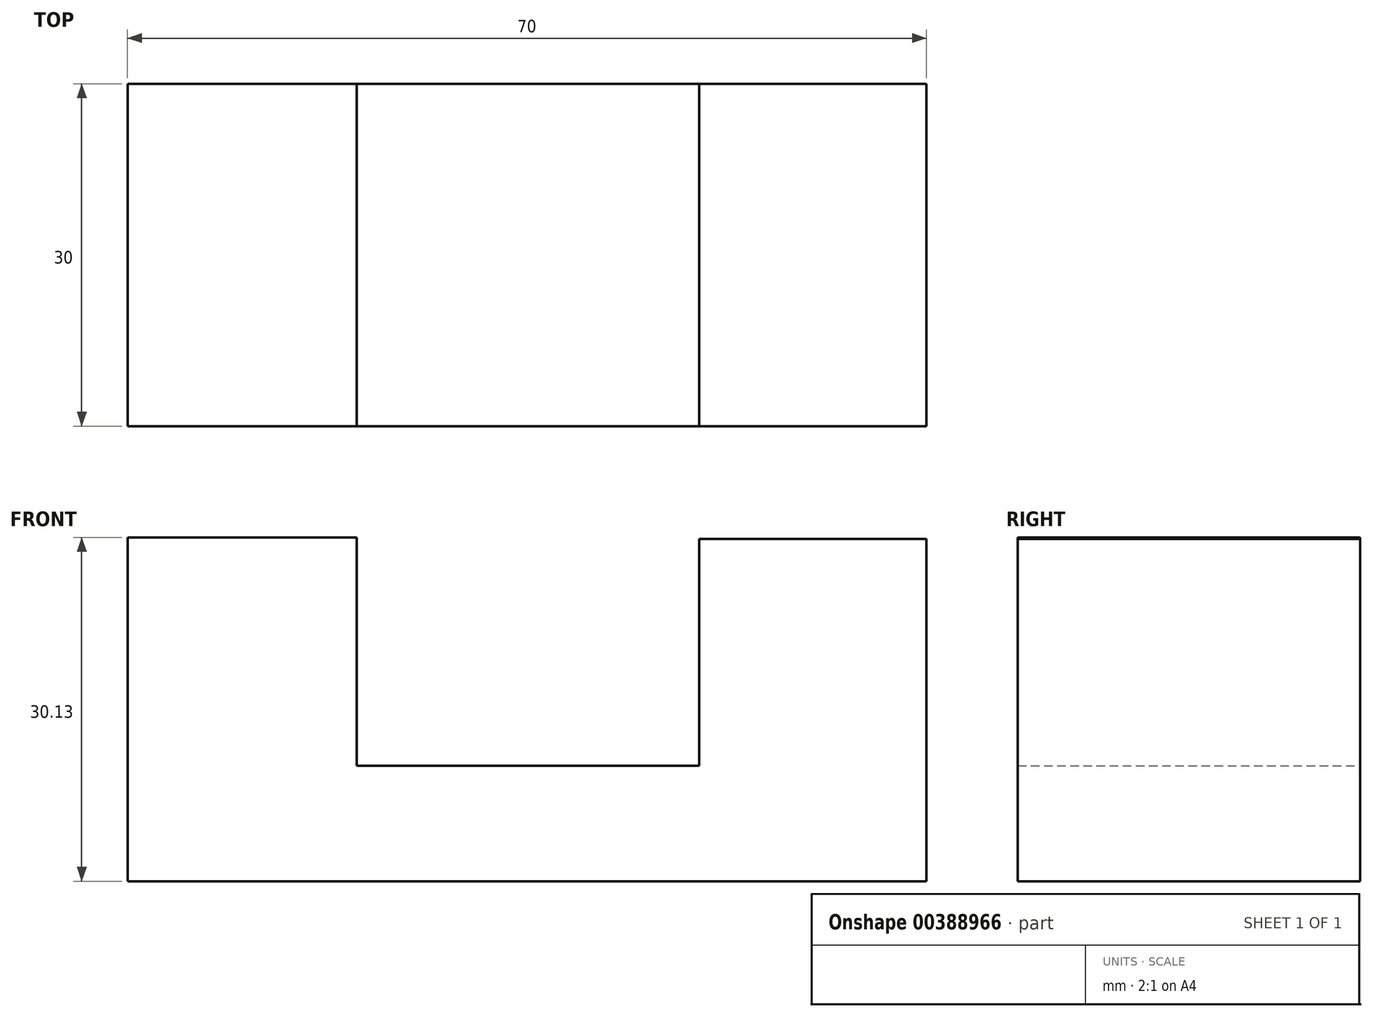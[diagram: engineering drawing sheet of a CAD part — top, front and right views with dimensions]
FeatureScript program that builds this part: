
annotation { "Feature Type Name" : "Feature", "Feature Type Description" : "" }
export const myFeature = defineFeature(function(context is Context, id is Id, definition is map)
    precondition{}
    {
        {
            var Q0;
            Q0=qCreatedBy(makeId("Front.planeOp"),FACE);
            var sketch = newSketch(context, id + "F0", { "sketchPlane" : qUnion([Q0])});
            skLineSegment(sketch, "E0", {"start": v(-41.37, 0) * mm, "end": v(28.63, 0) * mm});
            skLineSegment(sketch, "E1", {"start": v(28.63, 0) * mm, "end": v(28.63, 30) * mm});
            skLineSegment(sketch, "E2", {"start": v(28.63, 30) * mm, "end": v(17.7, 30) * mm});
            skLineSegment(sketch, "E3", {"start": v(17.7, 30) * mm, "end": v(8.72, 30) * mm});
            skLineSegment(sketch, "E4", {"start": v(17.7, 30) * mm, "end": v(17.7, 0) * mm});
            skLineSegment(sketch, "E5", {"start": v(-41.37, 0) * mm, "end": v(-41.37, 30.13) * mm});
            skLineSegment(sketch, "E6", {"start": v(-41.37, 30.13) * mm, "end": v(-30.14, 30.13) * mm});
            skLineSegment(sketch, "E7", {"start": v(-30.14, 30.13) * mm, "end": v(-21.28, 30.13) * mm});
            skLineSegment(sketch, "E8", {"start": v(-30.14, 30.13) * mm, "end": v(-30.14, 0) * mm});
            skLineSegment(sketch, "E9", {"start": v(-21.28, 30.13) * mm, "end": v(-21.28, 10.13) * mm});
            skLineSegment(sketch, "E10", {"start": v(-21.28, 10.13) * mm, "end": v(8.72, 10.13) * mm});
            skLineSegment(sketch, "E11", {"start": v(8.72, 10.13) * mm, "end": v(8.72, 30) * mm});
            skSolve(sketch);
        }
        {
            var Q0;
            {var subQ0=sQuery(id+"F0.wireOp",EDGE,"E5");Q0=makeQuery(id+"F0.imprint","IMPRINT",FACE,{"disambiguationData":[TD([[makeQuery(id+"F0.imprint","IMPRINT",EDGE,{"derivedFrom":subQ0}),-1.0]])]});}
            var Q1;
            {var subQ0=sQuery(id+"F0.wireOp",EDGE,"E1");Q1=makeQuery(id+"F0.imprint","IMPRINT",FACE,{"disambiguationData":[TD([[makeQuery(id+"F0.imprint","IMPRINT",EDGE,{"derivedFrom":subQ0}),1.0]])]});}
            var Q2;
            Q2=makeQuery(id+"F0.imprint","IMPRINT",FACE,{"disambiguationData":[TD([[makeQuery(id+"F0.imprint","IMPRINT",EDGE,{"derivedFrom":sQuery(id+"F0.wireOp",EDGE,"E3")}),1.0]])]});
            extrude(context, id + "F1", {"entities" : qUnion([Q0, Q1, Q2]), "depth" : 30 * mm});
        }
    });
